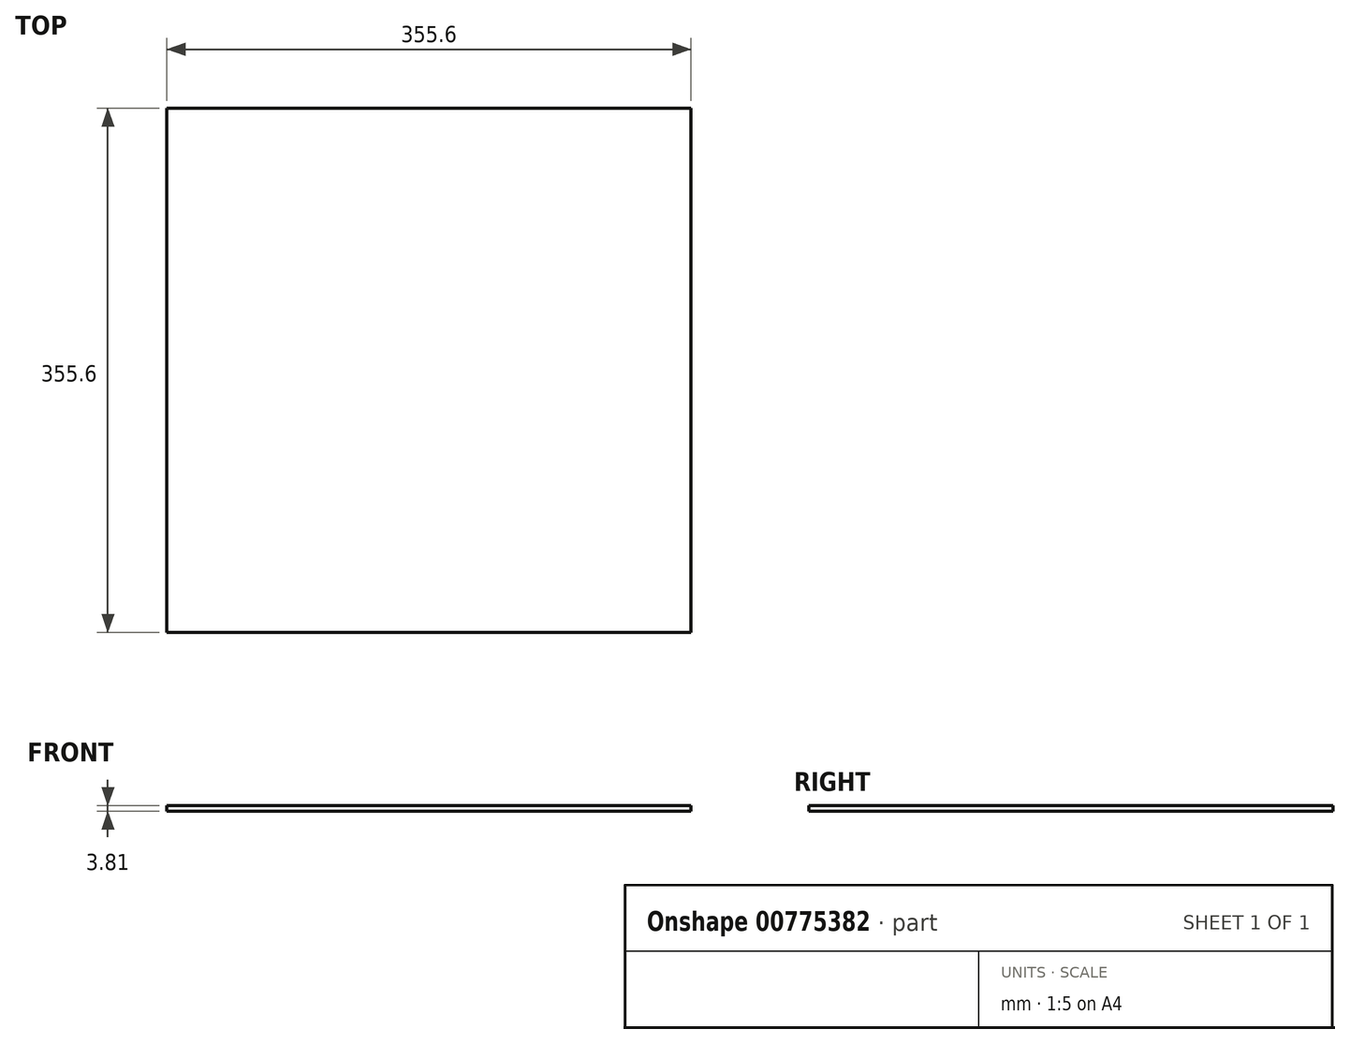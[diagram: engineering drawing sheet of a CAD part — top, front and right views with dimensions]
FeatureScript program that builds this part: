
annotation { "Feature Type Name" : "Feature", "Feature Type Description" : "" }
export const myFeature = defineFeature(function(context is Context, id is Id, definition is map)
    precondition{}
    {
        {
            var Q0;
            Q0=qCreatedBy(makeId("Top.planeOp"),FACE);
            var sketch = newSketch(context, id + "F0", { "sketchPlane" : qUnion([Q0])});
            skLineSegment(sketch, "E0.bottom", {"start": v(-177.8, 177.8) * mm, "end": v(177.8, 177.8) * mm});
            skLineSegment(sketch, "E0.top", {"start": v(-177.8, -177.8) * mm, "end": v(177.8, -177.8) * mm});
            skLineSegment(sketch, "E0.left", {"start": v(-177.8, 177.8) * mm, "end": v(-177.8, -177.8) * mm});
            skLineSegment(sketch, "E0.right", {"start": v(177.8, 177.8) * mm, "end": v(177.8, -177.8) * mm});
            skPoint(sketch, "E0.middle", {"position": v(0, 0) * mm});
            skSolve(sketch);
        }
        {
            var Q0;
            Q0 = qSketchRegion(id + "F0", true);
            extrude(context, id + "F1", {"entities" : qUnion([Q0]), "depth" : 3.8 * mm, "offsetDistance" : 25.4 * mm});
        }
    });
